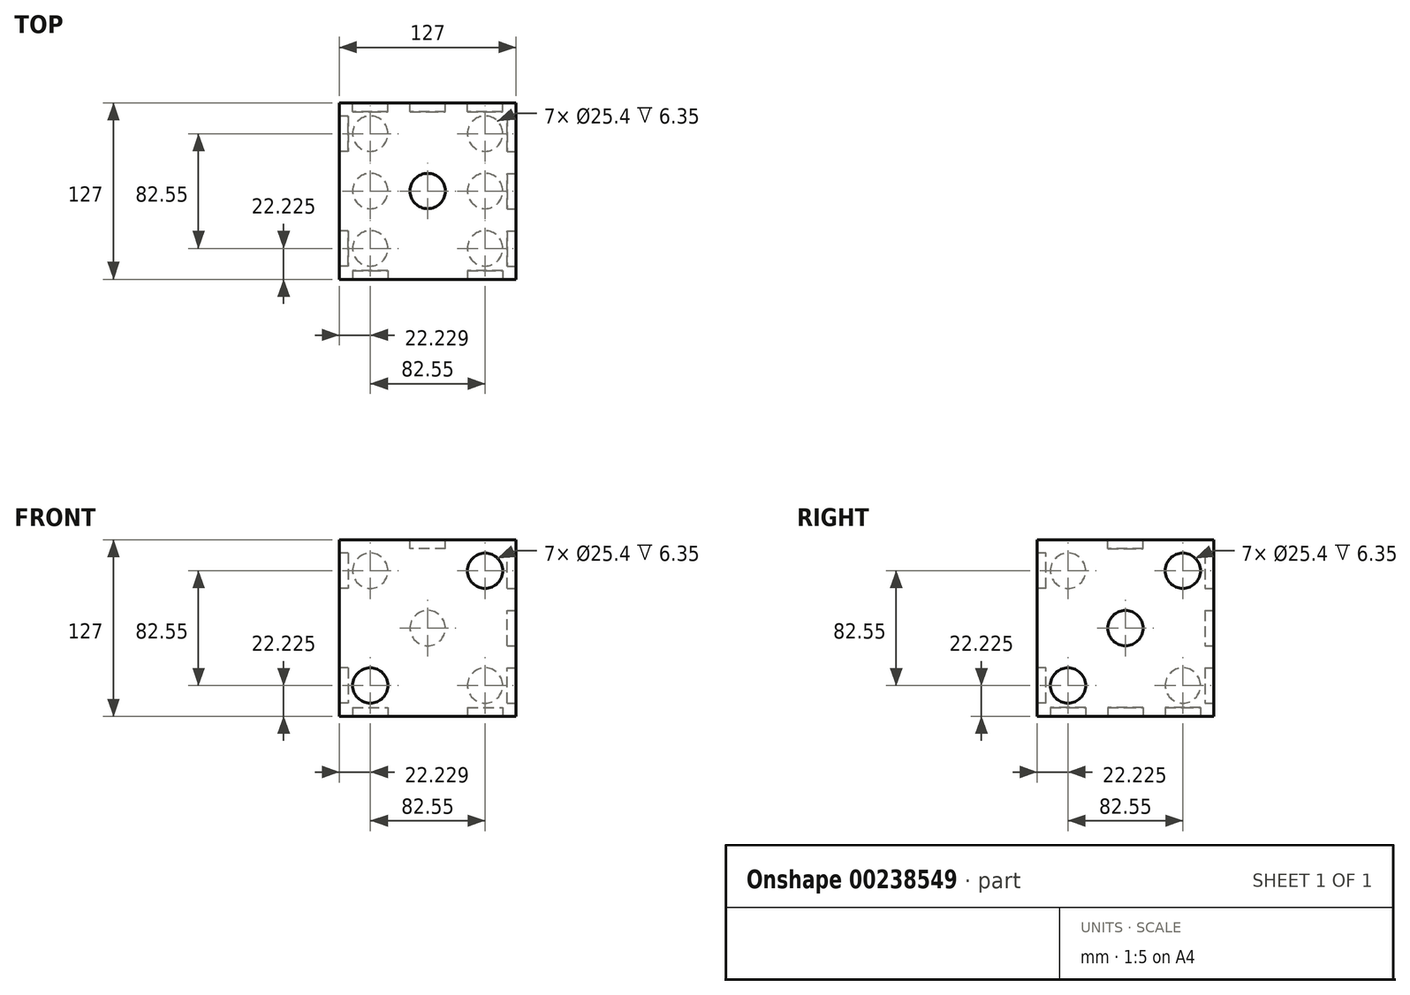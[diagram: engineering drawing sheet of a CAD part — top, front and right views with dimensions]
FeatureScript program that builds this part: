
annotation { "Feature Type Name" : "Feature", "Feature Type Description" : "" }
export const myFeature = defineFeature(function(context is Context, id is Id, definition is map)
    precondition{}
    {
        {
            var Q0;
            Q0=qCreatedBy(makeId("Top.planeOp"),FACE);
            var sketch = newSketch(context, id + "F0", { "sketchPlane" : qUnion([Q0])});
            skLineSegment(sketch, "E0.bottom", {"start": v(27.87, 4.99) * mm, "end": v(154.87, 4.99) * mm});
            skLineSegment(sketch, "E0.top", {"start": v(27.87, 131.99) * mm, "end": v(154.87, 131.99) * mm});
            skLineSegment(sketch, "E0.left", {"start": v(27.87, 4.99) * mm, "end": v(27.87, 131.99) * mm});
            skLineSegment(sketch, "E0.right", {"start": v(154.87, 4.99) * mm, "end": v(154.87, 131.99) * mm});
            skSolve(sketch);
        }
        {
            var Q0;
            Q0 = qSketchRegion(id + "F0", true);
            extrude(context, id + "F1", {"entities" : qUnion([Q0]), "depth" : 127 * mm});
        }
        {
            var Q0;
            Q0=makeQuery(id+"F1.opExtrude","CAP_FACE",FACE,{"disambiguationData":[OSD([sQuery(id+"F0.wireOp",EDGE,"E0.bottom"),sQuery(id+"F0.wireOp",EDGE,"E0.top"),sQuery(id+"F0.wireOp",EDGE,"E0.left"),sQuery(id+"F0.wireOp",EDGE,"E0.right")])],"isStart":false});
            var sketch = newSketch(context, id + "F2", { "sketchPlane" : qUnion([Q0])});
            skCircle(sketch, "E1", {"center": v(91.37, 68.49) * mm, "radius": 12.7 * mm});
            skSolve(sketch);
        }
        {
            var Q0;
            Q0 = qSketchRegion(id + "F2", true);
            extrude(context, id + "F3", {"entities" : qUnion([Q0]), "operationType" : NewBodyOperationType.REMOVE, "oppositeDirection" : true, "depth" : 6.35 * mm});
        }
        {
            var Q0;
            Q0=makeQuery(id+"F1.opExtrude","SWEPT_FACE",FACE,{"disambiguationData":[OSD([sQuery(id+"F0.wireOp",EDGE,"E0.bottom")])]});
            var sketch = newSketch(context, id + "F4", { "sketchPlane" : qUnion([Q0])});
            skCircle(sketch, "E2", {"center": v(50.1, 22.22) * mm, "radius": 12.7 * mm});
            skCircle(sketch, "E3", {"center": v(132.65, 104.78) * mm, "radius": 12.7 * mm});
            skSolve(sketch);
        }
        {
            var Q0;
            Q0 = qSketchRegion(id + "F4", true);
            extrude(context, id + "F5", {"entities" : qUnion([Q0]), "operationType" : NewBodyOperationType.REMOVE, "oppositeDirection" : true, "depth" : 6.35 * mm});
        }
        {
            var Q0;
            Q0=makeQuery(id+"F1.opExtrude","SWEPT_FACE",FACE,{"disambiguationData":[OSD([sQuery(id+"F0.wireOp",EDGE,"E0.right")])]});
            var sketch = newSketch(context, id + "F6", { "sketchPlane" : qUnion([Q0])});
            skCircle(sketch, "E4", {"center": v(68.49, 63.5) * mm, "radius": 12.7 * mm});
            skCircle(sketch, "E5", {"center": v(109.76, 104.78) * mm, "radius": 12.7 * mm});
            skCircle(sketch, "E6", {"center": v(27.21, 22.22) * mm, "radius": 12.7 * mm});
            skSolve(sketch);
        }
        {
            var Q0;
            Q0 = qSketchRegion(id + "F6", true);
            extrude(context, id + "F7", {"entities" : qUnion([Q0]), "operationType" : NewBodyOperationType.REMOVE, "oppositeDirection" : true, "depth" : 6.35 * mm});
        }
        {
            var Q0;
            Q0=makeQuery(id+"F1.opExtrude","SWEPT_FACE",FACE,{"disambiguationData":[OSD([sQuery(id+"F0.wireOp",EDGE,"E0.left")])]});
            var sketch = newSketch(context, id + "F8", { "sketchPlane" : qUnion([Q0])});
            skCircle(sketch, "E7", {"center": v(-109.76, 104.78) * mm, "radius": 12.7 * mm});
            skCircle(sketch, "E8", {"center": v(-27.21, 104.78) * mm, "radius": 12.7 * mm});
            skCircle(sketch, "E9", {"center": v(-109.76, 22.22) * mm, "radius": 12.7 * mm});
            skCircle(sketch, "E10", {"center": v(-27.21, 22.22) * mm, "radius": 12.7 * mm});
            skSolve(sketch);
        }
        {
            var Q0;
            Q0 = qSketchRegion(id + "F8", true);
            extrude(context, id + "F9", {"entities" : qUnion([Q0]), "operationType" : NewBodyOperationType.REMOVE, "oppositeDirection" : true, "depth" : 6.35 * mm});
        }
        {
            var Q0;
            Q0=makeQuery(id+"F1.opExtrude","SWEPT_FACE",FACE,{"disambiguationData":[OSD([sQuery(id+"F0.wireOp",EDGE,"E0.top")])]});
            var sketch = newSketch(context, id + "F10", { "sketchPlane" : qUnion([Q0])});
            skCircle(sketch, "E11", {"center": v(-132.65, 104.78) * mm, "radius": 12.7 * mm});
            skCircle(sketch, "E12", {"center": v(-50.1, 104.78) * mm, "radius": 12.7 * mm});
            skCircle(sketch, "E13", {"center": v(-132.65, 22.22) * mm, "radius": 12.7 * mm});
            skCircle(sketch, "E14", {"center": v(-50.1, 22.22) * mm, "radius": 12.7 * mm});
            skCircle(sketch, "E15", {"center": v(-91.37, 63.5) * mm, "radius": 12.7 * mm});
            skSolve(sketch);
        }
        {
            var Q0;
            Q0 = qSketchRegion(id + "F10", true);
            extrude(context, id + "F11", {"entities" : qUnion([Q0]), "operationType" : NewBodyOperationType.REMOVE, "oppositeDirection" : true, "depth" : 6.35 * mm});
        }
        {
            var Q0;
            Q0=makeQuery(id+"F1.opExtrude","CAP_FACE",FACE,{"disambiguationData":[OSD([sQuery(id+"F0.wireOp",EDGE,"E0.bottom"),sQuery(id+"F0.wireOp",EDGE,"E0.top"),sQuery(id+"F0.wireOp",EDGE,"E0.left"),sQuery(id+"F0.wireOp",EDGE,"E0.right")])],"isStart":true});
            var sketch = newSketch(context, id + "F12", { "sketchPlane" : qUnion([Q0])});
            skCircle(sketch, "E16", {"center": v(50.1, -27.21) * mm, "radius": 12.7 * mm});
            skCircle(sketch, "E17", {"center": v(132.65, -27.21) * mm, "radius": 12.7 * mm});
            skCircle(sketch, "E18", {"center": v(50.1, -68.49) * mm, "radius": 12.7 * mm});
            skCircle(sketch, "E19", {"center": v(132.65, -68.49) * mm, "radius": 12.7 * mm});
            skCircle(sketch, "E20", {"center": v(50.1, -109.76) * mm, "radius": 12.7 * mm});
            skCircle(sketch, "E21", {"center": v(132.65, -109.76) * mm, "radius": 12.7 * mm});
            skSolve(sketch);
        }
        {
            var Q0;
            Q0 = qSketchRegion(id + "F12", true);
            extrude(context, id + "F13", {"entities" : qUnion([Q0]), "operationType" : NewBodyOperationType.REMOVE, "oppositeDirection" : true, "depth" : 6.35 * mm});
        }
    });
